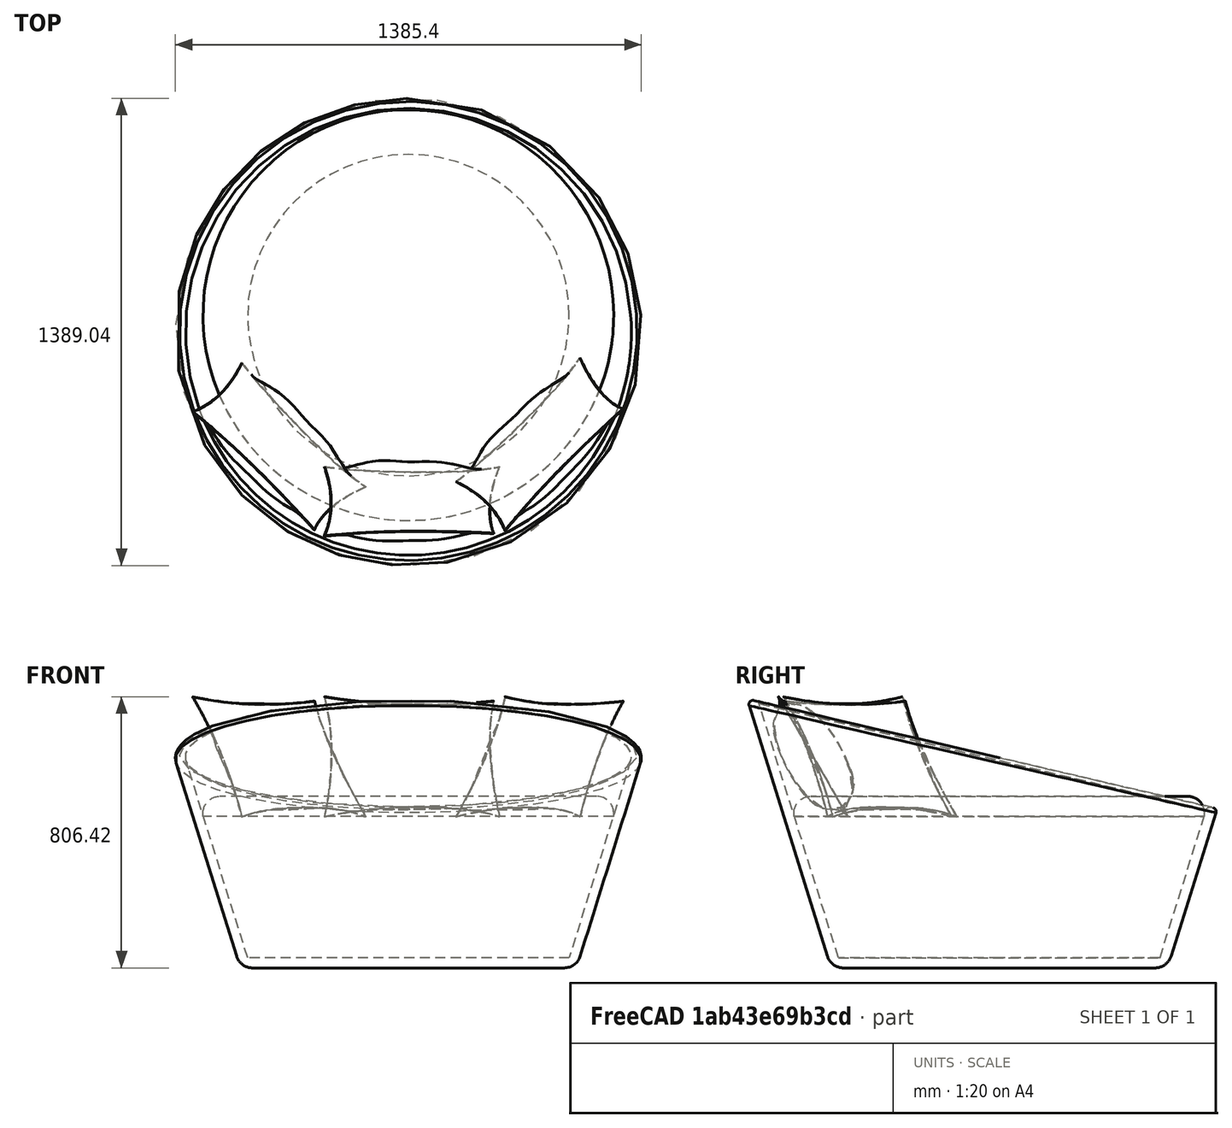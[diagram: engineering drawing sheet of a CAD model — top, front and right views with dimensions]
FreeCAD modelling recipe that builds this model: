
FCSTD DOCUMENT  (FreeCAD 0.21R33668 +26 (Git))
Label: Chaise
License: All rights reserved
objects: Sketcher::SketchObject×4, Part::FeaturePython×2, Part::Loft×1, Part::Thickness×1, Part::Extrusion×1, Part::MultiCommon×1, Part::Revolution×1, Part::Fillet×1, Part::Feature×1, Part::Compound×1
note: 14 computed .brp shape members not serialized (recipe doc carries the construction recipe); baked Part::Feature solids carry a one-line shape summary decoded from their .brp

FEATURE [Sketcher::SketchObject] Sketch
  FullyConstrained = true
  expr: Constraints[1] = <<Parametros Chaise>>.DiametroBase
  sketch-geometry (1):
    g0: Circle CenterX=0 CenterY=0 CenterZ=0 NormalX=0 NormalY=0 NormalZ=1 AngleXU=0 Radius=500
  constraints (2):
    c: Coincident(g0,g-1)
    c: Diameter(g0) = 1000
FEATURE [Sketcher::SketchObject] Sketch001
  FullyConstrained = true
  Placement = pos=(0,0,800) rot=(0,0,1;0rad)
  expr: .Placement.Base.z = <<Parametros Chaise>>.AlturaEscora
  expr: Constraints[1] = <<Parametros Chaise>>.DiametroTopo
  sketch-geometry (1):
    g0: Circle CenterX=0 CenterY=0 CenterZ=0 NormalX=0 NormalY=0 NormalZ=1 AngleXU=0 Radius=750
  constraints (2):
    c: Coincident(g0,g-1)
    c: Diameter(g0) = 1500
FEATURE [Part::Loft] Loft
  Closed = false
  MaxDegree = 5
  Ruled = false
  Sections = -> [Sketch001,Sketch]
  Solid = true
FEATURE [Part::Thickness] Thickness
  Faces = -> Loft [Face2]
  Intersection = false
  Join = 2
  Mode = 0
  SelfIntersection = false
  Value = -30
FEATURE [Part::FeaturePython] Point  label="Parametros Chaise"  # WARN: FeaturePython — macro-defined, semantics opaque (R4)
  AlturaAcento = 450
  AlturaEscora = 800
  DiametroBase = 1000
  DiametroTopo = 1500
  NumAlmofadas = 3
  RaioAlmofadas = 450
  X = 0
  Y = 0
  Z = 0
FEATURE [Sketcher::SketchObject] Sketch002
  FullyConstrained = true
  Placement = pos=(0,0,0) rot=(0.57735,0.57735,0.57735;2.0944rad)
  expr: Constraints[10] = <<Parametros Chaise>>.AlturaAcento
  expr: Constraints[7] = <<Parametros Chaise>>.DiametroTopo
  expr: Constraints[9] = <<Parametros Chaise>>.AlturaEscora
  sketch-geometry (4):
    g0: LineSegment StartX=-750 StartY=800 StartZ=0 EndX=-750 EndY=0 EndZ=0
    g1: LineSegment StartX=-750 StartY=800 StartZ=0 EndX=750 EndY=450 EndZ=0
    g2: LineSegment StartX=750 StartY=450 StartZ=0 EndX=750 EndY=0 EndZ=0
    g3: LineSegment StartX=-750 StartY=0 StartZ=0 EndX=750 EndY=0 EndZ=0
  constraints (11):
    c: Coincident(g1,g0)
    c: Coincident(g2,g1)
    c: PointOnObject(g2,g-1)
    c: Vertical(g2)
    c: Coincident(g3,g0)
    c: Coincident(g3,g2)
    c: Vertical(g0)
    c: DistanceX(g3,g3) = 1500
    c: Symmetric(g0,g2,g-2)
    c: DistanceY(g0,g0) = 800
    c: DistanceY(g2,g2) = 450
FEATURE [Part::Extrusion] Extrude
  Base = -> Sketch002
  Dir = (1,0,0)
  DirMode = 2
  FaceMakerClass = Part::FaceMakerBullseye
  LengthFwd = 750
  LengthRev = 750
  Solid = true
  Symmetric = false
  expr: LengthFwd = <<Parametros Chaise>>.DiametroTopo / 2
  expr: LengthRev = <<Parametros Chaise>>.DiametroTopo / 2
FEATURE [Part::MultiCommon] Common
  Shapes = -> [Thickness,Extrude]
FEATURE [Sketcher::SketchObject] Sketch003  label="rascunhoEstofado"
  FullyConstrained = true
  Placement = pos=(0,0,0) rot=(0.57735,0.57735,0.57735;2.0944rad)
  expr: .Constraints.DiametroEstofado = <<Parametros Chaise>>.AlturaAcento * (<<Parametros Chaise>>.DiametroTopo - <<Parametros Chaise>>.DiametroBase) / <<Parametros Chaise>>.AlturaEscora + <<Parametros Chaise>>.DiametroBase - 6 cm
  sketch-geometry (7):
    g0: LineSegment StartX=-610.625 StartY=0 StartZ=0 EndX=610.625 EndY=0 EndZ=0
    g1: LineSegment StartX=610.625 StartY=0 StartZ=0 EndX=610.625 EndY=10 EndZ=0
    g2: LineSegment StartX=0 StartY=60 StartZ=0 EndX=560.625 EndY=60 EndZ=0
    g3: ArcOfCircle CenterX=560.625 CenterY=10 CenterZ=0 NormalX=0 NormalY=0 NormalZ=1 AngleXU=0 Radius=50 StartAngle=0 EndAngle=1.5708
    g4: GeomPoint X=610.625 Y=60 Z=0
    g5: LineSegment StartX=0 StartY=60 StartZ=0 EndX=0 EndY=0 EndZ=0
    g6: LineSegment StartX=0 StartY=0 StartZ=0 EndX=610.625 EndY=0 EndZ=0
  constraints (17):
    c: Horizontal(g0)
    c: Symmetric(g0,g0,g-1)
    c: DistanceX(g0,g0) = 1221.25  'DiametroEstofado'
    c: Coincident(g1,g0)
    c: Vertical(g1)
    c: PointOnObject(g4,g2)
    c: PointOnObject(g4,g1)
    c: Tangent(g2,g3) = 1.5708
    c: Tangent(g1,g3) = -1.5708
    c: PointOnObject(g2,g-2)
    c: DistanceY(g1,g4) = 60
    c: Radius(g3) = 50
    c: Horizontal(g2)
    c: Coincident(g5,g2)
    c: Coincident(g5,g-1)
    c: Coincident(g6,g5)
    c: Coincident(g6,g1)
FEATURE [Part::Revolution] Revolve  label="Estofado"
  Angle = 360
  Axis = (0,0,1)
  Base = (0,0,0)
  FaceMakerClass = Part::FaceMakerBullseye
  Placement = pos=(-1.68e-13,2.87e-13,450) rot=(0,0,-1;1.5708rad)
  Solid = true
  Source = -> Sketch003
  Symmetric = false
  expr: .Placement.Base.z = <<Parametros Chaise>>.AlturaAcento
FEATURE [Part::Fillet] Fillet
  Base = -> Common
  Edges = 4 edges: [Edge1 r=12,Edge3 r=50,Edge4 r=12,Edge5 r=12]
FEATURE [Part::Feature] Clone001  label="Almofada002"
  Placement = pos=(-250,-450,450) rot=(1,0,0;0.523599rad)
  shape: bbox 577.7 x 899.7 x 668.9 mm, 16 faces, 2 solids (baked)
  expr: .Placement.Base.y = -<<Parametros Chaise>>.RaioAlmofadas
  expr: .Placement.Base.z = <<Parametros Chaise>>.AlturaAcento
FEATURE [Part::FeaturePython] Array  # Draft array (typed FeaturePython)
  Angle = 90
  ArrayType = 1
  Axis = (0,0,1)
  Base = -> Clone001
  Center = (0,0,0)
  Count = 3
  Fuse = false
  IntervalAxis = (0,0,0)
  IntervalX = (100,0,0)
  IntervalY = (0,100,0)
  IntervalZ = (0,0,100)
  NumberCircles = 3
  NumberPolar = 3
  NumberX = 2
  NumberY = 1
  NumberZ = 1
  Placement = pos=(-1.93e-13,3.5e-14,0) rot=(0,0,-1;0.785398rad)
  RadialDistance = 50
  Symmetry = 1
  TangentialDistance = 25
  expr: NumberPolar = <<Parametros Chaise>>.NumAlmofadas
FEATURE [Part::Compound] Compound  label="Chaise"
  Links = -> [Point,Revolve,Fillet,Array]
